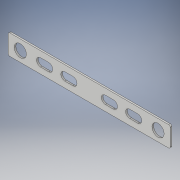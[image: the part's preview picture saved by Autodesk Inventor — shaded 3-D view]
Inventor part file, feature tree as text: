
AUTODESK INVENTOR PART (.ipt)
format: ipt  version: 2019 (Build 230136000, 136)  size: 148,480 bytes
history: native  units: mm
features: extrude x2, sketch x2, plane x1, mirror x1
ambient origin geometry x8: Origin, YZ Plane, XZ Plane, XY Plane, X Axis, Y Axis, Z Axis, Center Point
bodies: Solid1 (feature_tree)
feature tree (6):
  extrude  "Extrusion1"  Depth=25.0mm
  extrude  "Extrusion2"  Depth=2.0mm TaperAngle=0.0deg
  plane  "Work Plane1"
  mirror  "Mirror1"
  sketch  "Sketch1"  dims[d0=200.0mm d1=25.0mm]
  sketch  "Sketch2"  dims[d2=2.0mm d3=2.0mm d4=0.0mm d5=15.0mm d6=15.0mm d7=20.0mm d8=10.0mm d9=20.0mm d10=30.0mm d11=25.0mm d12=2.0mm d13=0.0mm d14=-100.0mm]
